# Revit family: PRD_AR_ShwrSts_MEDCAREFoldableShowerSeat_MEDC0013
name_source: partatom
category: Specialty Equipment
units: mm (PartAtom-declared; Revit-internal decimal feet)

## family parameters
Cut with Voids When Loaded = No
Enable Cutting in Views = No
Host = Face
Maintain Annotation Orientation = No
OmniClass Number = 23.45.05.14.11.17
OmniClass Title = Shower/Bath Seats
Part Type = Normal
Room Calculation Point = No
Round Connector Dimension = Use Diameter
Shared = No

## types (1)
- MEDC0013
    AssetType = Fixed
    BIMObjectName = PRD_AR_ShowerSeats_MEDCAREFoldableShowerSeat_MEDC0013
    Back = yes
    BodyMaterial = PRD_AR_StainlessSteel_SatinFinished_BasaltGrey
    Category = Pr_40_20_06_83, Shower seats
    Color = basalt grey
    Default Elevation = 1200 mm
    Description = MEDCARE foldable shower seat for wall mounting, with continuous and ergonomically shaped seat made of polyurethane, colour basalt grey, with integrated reinforcement frame, protection against accidental folding down, wall bracket made of stainless steel, surface satin finished, load capacity up to 150 kg, mounting material to be provided by the client.
    Diameter = 0 mm  [stored 0 ft]
    Export Type to IFC As = IfcFurnitureType
    Features = Load capacity up to 150 kg.
    Finish = satin finished
    Height = 0 mm  [stored 0 ft]
    HiddenFixing = yes
    IfcExportAs = IfcFurnitureType
    IfcExportType = USERDEFINED
    IsExternal = FALSE
    Manufacturer = KWC Group Management AG
    ManufacturerName = KWC Group Management AG
    ManufacturerURL = www.kwc-professional.com
    Material = stainless steel
    Model = MEDC0013
    ModelNumber = 3600003783
    ModelReference = MEDC0013
    NBSDescription = Shower seats
    NBSReference = 45-35-72/352
    Name = MEDCARE Foldable shower seat MEDC0013
    NominalDepth = 458 mm
    NominalHeight = 90 mm  [stored 0.295276 ft]
    NominalWidth = 450 mm  [stored 1.47638 ft]
    OverallDepth = 458 mm
    OverallHeight = 95 mm
    OverallWidth = 450 mm
    ProductInformation = http://pim.kwc.com
    Size = 450 x 90 x 458 mm (W x H x D)
    Status = New
    Type IFC Predefined Type = USERDEFINED
    TypeOfFixing = screw
    TypeOfGrabRail = shower seat
    TypeOfMounting = wall mounting
    URL = www.kwc-professional.com
    Uniclass2015Code = Pr_40_20_06_83
    Uniclass2015Title = Shower seats
    Uniclass2015Version = Products v1.36
    Version = 1

note: [stored X ft] marks values corroborated as IEEE doubles in the binary element streams (Revit-internal decimal feet)

## geometry (parser evidence)
native form markers: Sweep x9
no freeform markers — native parametric forms only
